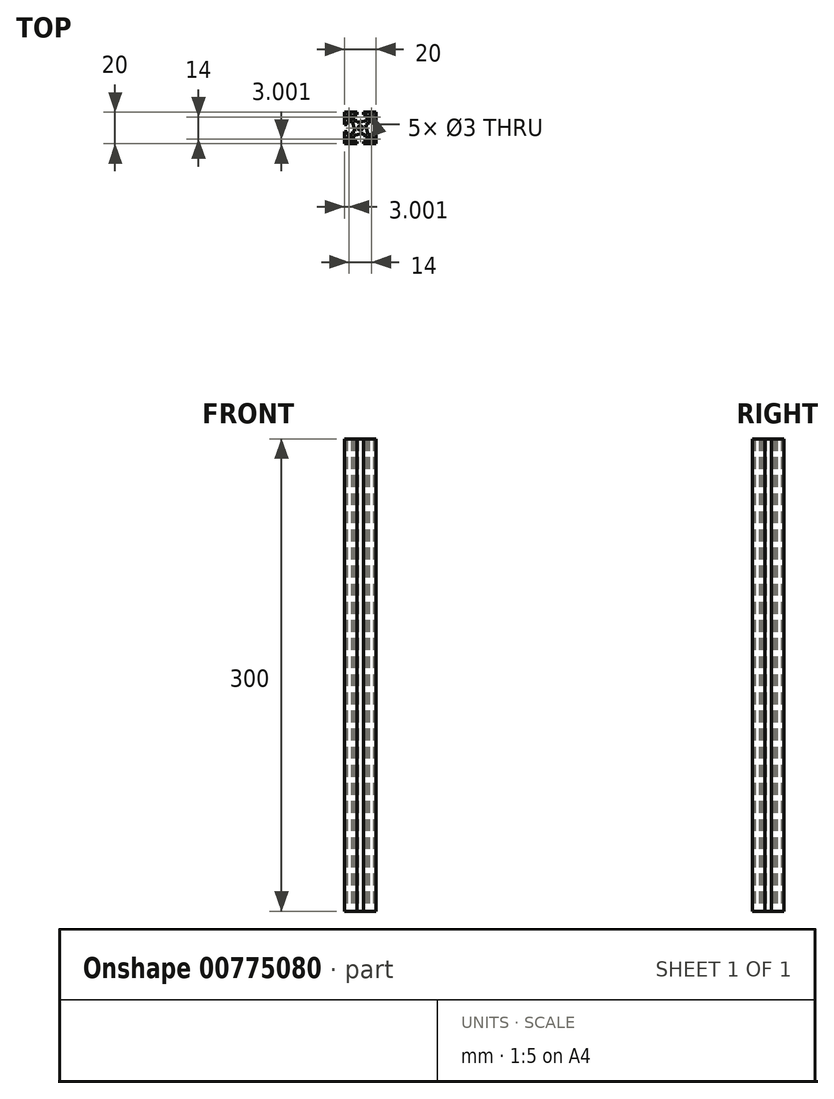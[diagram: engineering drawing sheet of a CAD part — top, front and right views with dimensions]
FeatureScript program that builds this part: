
annotation { "Feature Type Name" : "Feature", "Feature Type Description" : "" }
export const myFeature = defineFeature(function(context is Context, id is Id, definition is map)
    precondition{}
    {
        {
            var Q0;
            Q0=qCreatedBy(makeId("Top.planeOp"),FACE);
            var sketch = newSketch(context, id + "F0", { "sketchPlane" : qUnion([Q0])});
            skLineSegment(sketch, "E0.bottom", {"start": v(-9.98, 10.12) * mm, "end": v(-2.13, 10.12) * mm});
            skLineSegment(sketch, "E0.top", {"start": v(-9.98, -9.88) * mm, "end": v(-2.13, -9.88) * mm});
            skLineSegment(sketch, "E0.left", {"start": v(-9.98, 10.12) * mm, "end": v(-9.98, 2.27) * mm});
            skLineSegment(sketch, "E0.right", {"start": v(10.02, 10.12) * mm, "end": v(10.02, 2.27) * mm});
            skLineSegment(sketch, "E1.0", {"start": v(-9.98, -6.88) * mm, "end": v(10.02, -6.88) * mm, "construction": true});
            skLineSegment(sketch, "E2.0", {"start": v(-9.98, 7.12) * mm, "end": v(10.02, 7.12) * mm, "construction": true});
            skPoint(sketch, "E3.endSnap0", {"position": v(0.02, -6.88) * mm});
            skLineSegment(sketch, "E4.0", {"start": v(7.02, -9.88) * mm, "end": v(7.02, 10.12) * mm, "construction": true});
            skLineSegment(sketch, "E5.0", {"start": v(-6.98, -9.88) * mm, "end": v(-6.98, 10.12) * mm, "construction": true});
            skLineSegment(sketch, "E6.0", {"start": v(-4.13, 8.62) * mm, "end": v(-2.13, 8.62) * mm});
            skLineSegment(sketch, "E7.0", {"start": v(-4.13, 4.92) * mm, "end": v(-2.13, 4.92) * mm});
            skLineSegment(sketch, "E8.trimOffspring", {"start": v(2.17, 8.62) * mm, "end": v(2.17, 10.12) * mm});
            skLineSegment(sketch, "E9.trimOffspring", {"start": v(4.17, 4.92) * mm, "end": v(4.17, 8.62) * mm});
            skLineSegment(sketch, "E10.MirrorCS", {"start": v(-2.13, 8.62) * mm, "end": v(-2.13, 10.12) * mm});
            skLineSegment(sketch, "E11", {"start": v(-2.13, 3.42) * mm, "end": v(4.17, 4.92) * mm});
            skLineSegment(sketch, "E12.trimOffspring", {"start": v(-2.13, 4.92) * mm, "end": v(-2.13, 3.42) * mm});
            skLineSegment(sketch, "E13.MirrorCS", {"start": v(-4.13, 4.92) * mm, "end": v(-4.13, 8.62) * mm});
            skLineSegment(sketch, "E14.trimOffspring", {"start": v(2.17, 8.62) * mm, "end": v(4.17, 8.62) * mm});
            skLineSegment(sketch, "E15.trimOffspring", {"start": v(2.17, 10.12) * mm, "end": v(10.02, 10.12) * mm});
            skLineSegment(sketch, "E16.1.0", {"start": v(4.82, 4.27) * mm, "end": v(4.82, 2.27) * mm});
            skLineSegment(sketch, "E16.1.1", {"start": v(8.52, 4.27) * mm, "end": v(8.52, 2.27) * mm});
            skLineSegment(sketch, "E16.1.2", {"start": v(3.32, 2.27) * mm, "end": v(4.82, -4.03) * mm});
            skLineSegment(sketch, "E16.1.3", {"start": v(8.52, 2.27) * mm, "end": v(10.02, 2.27) * mm});
            skLineSegment(sketch, "E16.1.4", {"start": v(4.82, -4.03) * mm, "end": v(8.52, -4.03) * mm});
            skLineSegment(sketch, "E16.1.5", {"start": v(4.82, 4.27) * mm, "end": v(8.52, 4.27) * mm});
            skLineSegment(sketch, "E16.1.6", {"start": v(4.82, 2.27) * mm, "end": v(3.32, 2.27) * mm});
            skLineSegment(sketch, "E16.1.7", {"start": v(8.52, -2.03) * mm, "end": v(8.52, -4.03) * mm});
            skLineSegment(sketch, "E16.1.8", {"start": v(8.52, -2.03) * mm, "end": v(10.02, -2.03) * mm});
            skLineSegment(sketch, "E16.2.0", {"start": v(4.17, -4.68) * mm, "end": v(2.17, -4.68) * mm});
            skLineSegment(sketch, "E16.2.1", {"start": v(4.17, -8.38) * mm, "end": v(2.17, -8.38) * mm});
            skLineSegment(sketch, "E16.2.2", {"start": v(2.17, -3.18) * mm, "end": v(-4.13, -4.68) * mm});
            skLineSegment(sketch, "E16.2.3", {"start": v(2.17, -8.38) * mm, "end": v(2.17, -9.88) * mm});
            skLineSegment(sketch, "E16.2.4", {"start": v(-4.13, -4.68) * mm, "end": v(-4.13, -8.38) * mm});
            skLineSegment(sketch, "E16.2.5", {"start": v(4.17, -4.68) * mm, "end": v(4.17, -8.38) * mm});
            skLineSegment(sketch, "E16.2.6", {"start": v(2.17, -4.68) * mm, "end": v(2.17, -3.18) * mm});
            skLineSegment(sketch, "E16.2.7", {"start": v(-2.13, -8.38) * mm, "end": v(-4.13, -8.38) * mm});
            skLineSegment(sketch, "E16.2.8", {"start": v(-2.13, -8.38) * mm, "end": v(-2.13, -9.88) * mm});
            skPoint(sketch, "E16.center", {"position": v(0.02, 0.12) * mm});
            skLineSegment(sketch, "E17.trimOffspring", {"start": v(10.02, -2.03) * mm, "end": v(10.02, -9.88) * mm});
            skLineSegment(sketch, "E18.trimOffspring", {"start": v(2.17, -9.88) * mm, "end": v(10.02, -9.88) * mm});
            skPoint(sketch, "E19.1.7", {"position": v(-4.93, -4.83) * mm});
            skLineSegment(sketch, "E19.2.0", {"start": v(-8.48, 2.27) * mm, "end": v(-9.98, 2.27) * mm});
            skLineSegment(sketch, "E19.2.1", {"start": v(-8.48, -4.03) * mm, "end": v(-8.48, -2.03) * mm});
            skLineSegment(sketch, "E19.2.2", {"start": v(-4.78, 4.27) * mm, "end": v(-8.48, 4.27) * mm});
            skLineSegment(sketch, "E19.2.3", {"start": v(-4.78, -2.03) * mm, "end": v(-3.28, -2.03) * mm});
            skLineSegment(sketch, "E19.2.4", {"start": v(-8.48, -2.03) * mm, "end": v(-9.98, -2.03) * mm});
            skLineSegment(sketch, "E19.2.5", {"start": v(-8.48, 2.27) * mm, "end": v(-8.48, 4.27) * mm});
            skLineSegment(sketch, "E19.2.6", {"start": v(-4.78, -4.03) * mm, "end": v(-4.78, -2.03) * mm});
            skPoint(sketch, "E19.2.7", {"position": v(-6.98, 0.12) * mm});
            skLineSegment(sketch, "E19.2.8", {"start": v(-3.28, -2.03) * mm, "end": v(-4.78, 4.27) * mm});
            skLineSegment(sketch, "E19.2.9", {"start": v(-4.78, -4.03) * mm, "end": v(-8.48, -4.03) * mm});
            skLineSegment(sketch, "E20.trimOffspring", {"start": v(-9.98, -2.03) * mm, "end": v(-9.98, -9.88) * mm});
            skCircle(sketch, "E21", {"center": v(-6.98, 7.12) * mm, "radius": 1.5 * mm});
            skCircle(sketch, "E22", {"center": v(7.02, 7.12) * mm, "radius": 1.5 * mm});
            skCircle(sketch, "E23", {"center": v(7.02, -6.88) * mm, "radius": 1.5 * mm});
            skCircle(sketch, "E24", {"center": v(-6.98, -6.88) * mm, "radius": 1.5 * mm});
            skCircle(sketch, "E25", {"center": v(0.02, 0.12) * mm, "radius": 1.5 * mm});
            skSolve(sketch);
        }
        {
            var Q0;
            Q0=makeQuery(id+"F0.imprint","IMPRINT",FACE,{"disambiguationData":[TD([[makeQuery(id+"F0.imprint","IMPRINT",EDGE,{"derivedFrom":sQuery(id+"F0.wireOp",EDGE,"E0.bottom")}),-1.0]])]});
            extrude(context, id + "F1", {"entities" : qUnion([Q0]), "depth" : 300 * mm, "offsetDistance" : 25 * mm});
        }
    });
